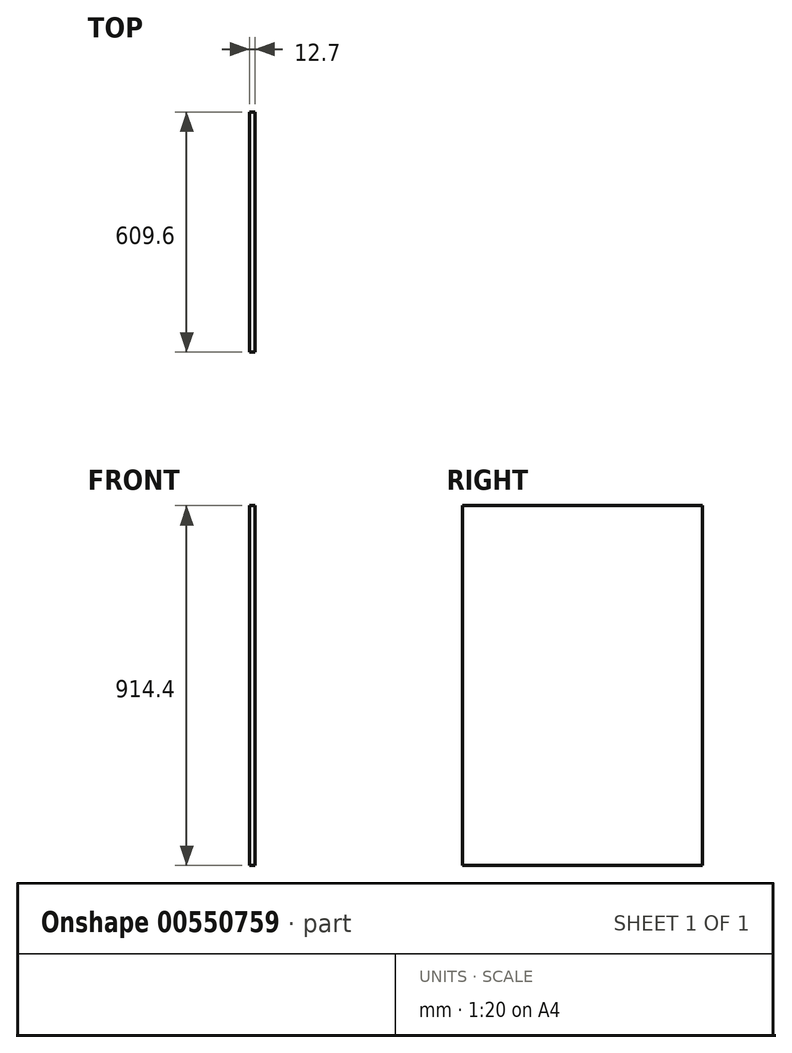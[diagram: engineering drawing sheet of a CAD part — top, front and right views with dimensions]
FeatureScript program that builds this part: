
annotation { "Feature Type Name" : "Feature", "Feature Type Description" : "" }
export const myFeature = defineFeature(function(context is Context, id is Id, definition is map)
    precondition{}
    {
        {
            var Q0;
            Q0=qCreatedBy(makeId("Right.planeOp"),FACE);
            var sketch = newSketch(context, id + "F0", { "sketchPlane" : qUnion([Q0])});
            skLineSegment(sketch, "E0.bottom", {"start": v(0, 0) * mm, "end": v(609.6, 0) * mm});
            skLineSegment(sketch, "E0.top", {"start": v(0, 914.4) * mm, "end": v(609.6, 914.4) * mm});
            skLineSegment(sketch, "E0.left", {"start": v(0, 0) * mm, "end": v(0, 914.4) * mm});
            skLineSegment(sketch, "E0.right", {"start": v(609.6, 0) * mm, "end": v(609.6, 914.4) * mm});
            skSolve(sketch);
        }
        {
            var Q0;
            Q0 = qSketchRegion(id + "F0", true);
            extrude(context, id + "F1", {"entities" : qUnion([Q0]), "depth" : 12.7 * mm, "offsetDistance" : 25.4 * mm});
        }
    });
